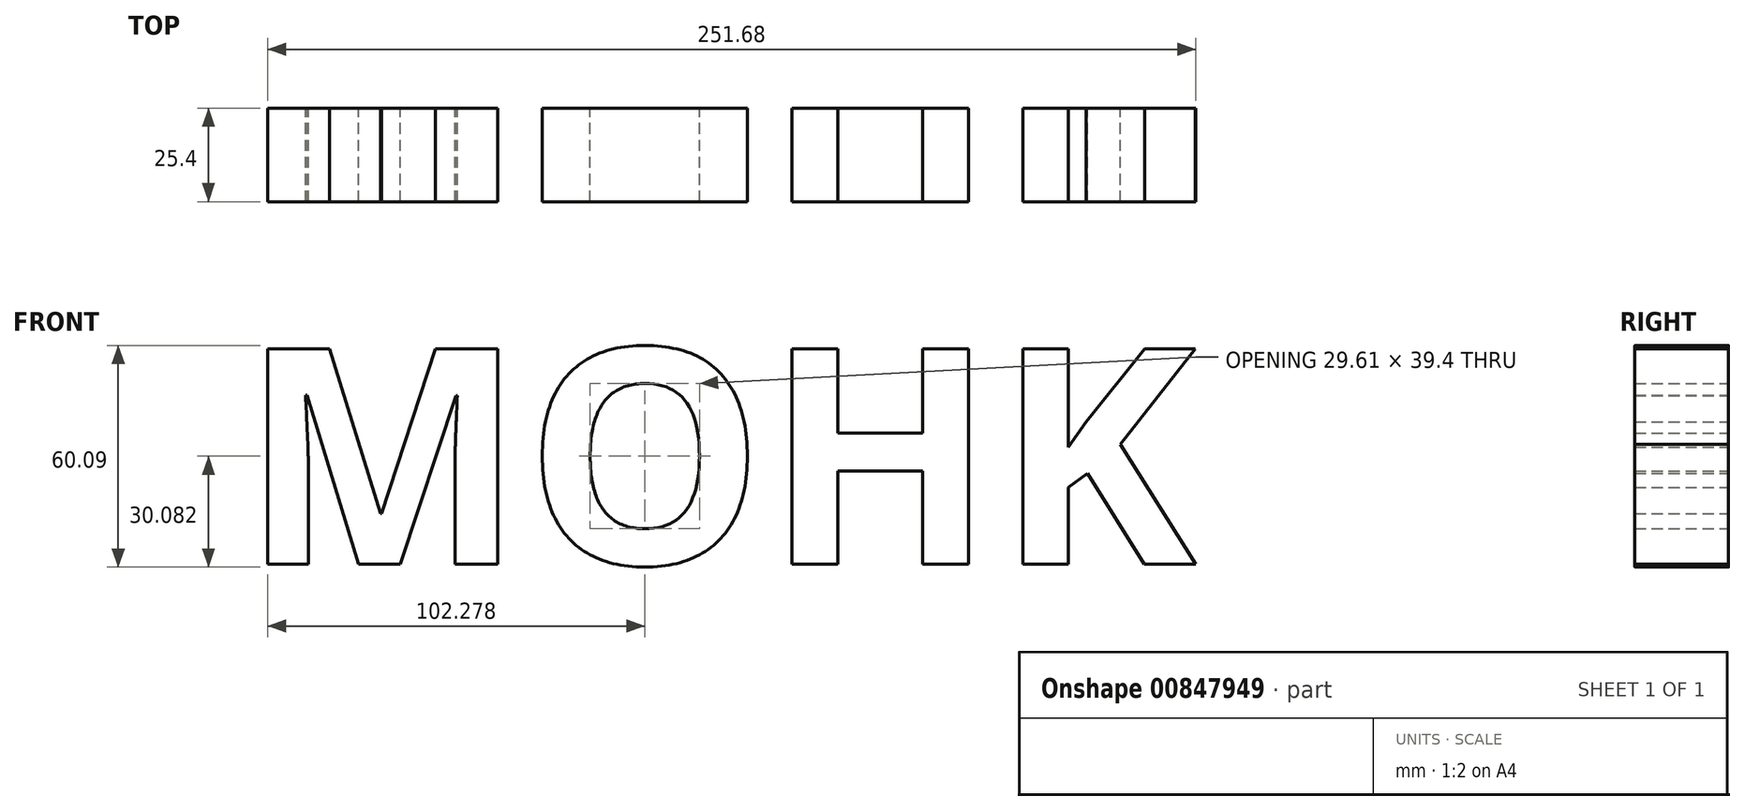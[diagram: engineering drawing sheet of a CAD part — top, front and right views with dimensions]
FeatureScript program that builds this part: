
annotation { "Feature Type Name" : "Feature", "Feature Type Description" : "" }
export const myFeature = defineFeature(function(context is Context, id is Id, definition is map)
    precondition{}
    {
        {
            var Q0;
            Q0=qCreatedBy(makeId("Front.planeOp"),FACE);
            var sketch = newSketch(context, id + "F0", { "sketchPlane" : qUnion([Q0])});
            skText(sketch, "E0", { "text": "MOHK", "fontName": "OpenSans-Bold.ttf"});
            const initialGuessF0  = {"E0": [-0.19965, -0.007, 1, 0, 0.05887]};
            skSetInitialGuess(sketch, initialGuessF0);
            skSolve(sketch);
        }
        {
            var Q0;
            Q0 = qSketchRegion(id + "F0", true);
            extrude(context, id + "F1", {"entities" : qUnion([Q0]), "depth" : 25.4 * mm, "offsetDistance" : 25.4 * mm});
        }
    });
